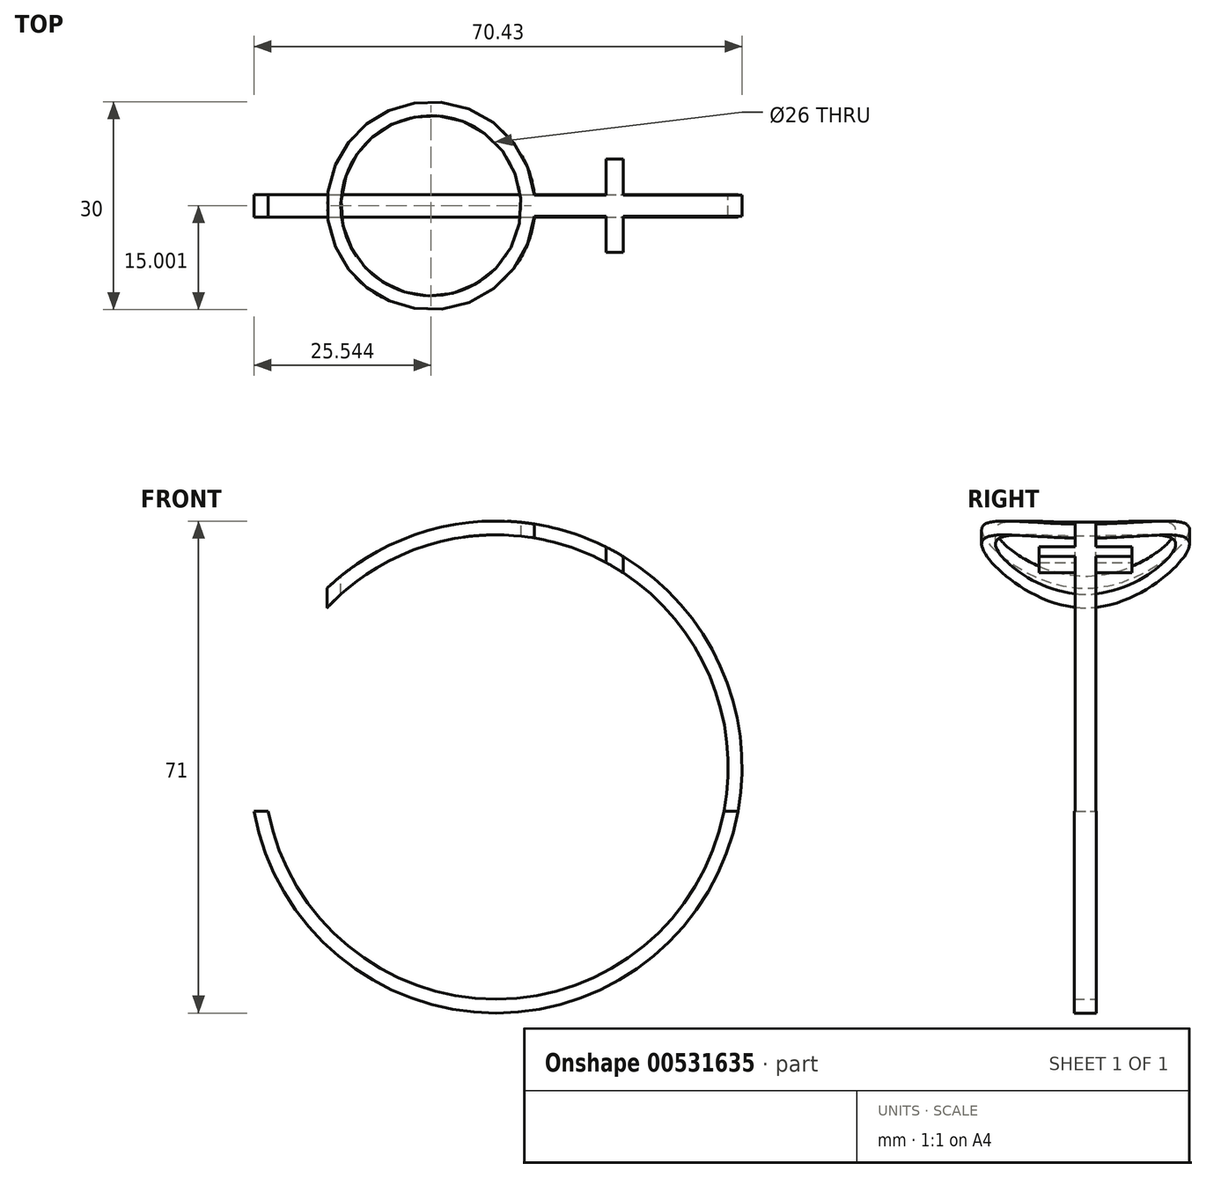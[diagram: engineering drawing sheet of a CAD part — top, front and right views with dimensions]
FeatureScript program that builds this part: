
annotation { "Feature Type Name" : "Feature", "Feature Type Description" : "" }
export const myFeature = defineFeature(function(context is Context, id is Id, definition is map)
    precondition{}
    {
        {
            var Q0;
            Q0=qCreatedBy(makeId("Front.planeOp"),FACE);
            var sketch = newSketch(context, id + "F0", { "sketchPlane" : qUnion([Q0])});
            skCircle(sketch, "E0", {"center": v(0, 0) * mm, "radius": 33.5 * mm});
            skCircle(sketch, "E1", {"center": v(0, 0) * mm, "radius": 35.5 * mm});
            skSolve(sketch);
        }
        {
            var Q0;
            Q0=makeQuery(id+"F0.imprint","IMPRINT",FACE,{"disambiguationData":[TD([[makeQuery(id+"F0.imprint","IMPRINT",EDGE,{"derivedFrom":sQuery(id+"F0.wireOp",EDGE,"E0")}),-1.0]])]});
            extrude(context, id + "F1", {"entities" : qUnion([Q0]), "depth" : 50.8 * mm, "offsetDistance" : 25.4 * mm});
        }
        {
            var Q0;
            Q0=qCreatedBy(makeId("Top.planeOp"),FACE);
            cPlane(context, id + "F2", {"entities" : qUnion([Q0]), "cplaneType" : CPlaneType.OFFSET, "offset" : 38.1 * mm, "width" : 152.4 * mm, "height" : 152.4 * mm});
        }
        {
            var Q0;
            Q0=qCreatedBy(id+"F2.planeOp",FACE);
            var sketch = newSketch(context, id + "F3", { "sketchPlane" : qUnion([Q0])});
            skCircle(sketch, "E2", {"center": v(-9.39, -26.8) * mm, "radius": 15 * mm});
            skCircle(sketch, "E3", {"center": v(-9.39, -26.8) * mm, "radius": 13 * mm});
            skLineSegment(sketch, "E4", {"start": v(5.61, -26.8) * mm, "end": v(11.46, -26.8) * mm});
            skLineSegment(sketch, "E5", {"start": v(5.54, -28.3) * mm, "end": v(15.85, -28.3) * mm});
            skLineSegment(sketch, "E6", {"start": v(15.85, -28.3) * mm, "end": v(15.85, -33.5) * mm});
            skLineSegment(sketch, "E7", {"start": v(15.85, -33.5) * mm, "end": v(18.35, -33.5) * mm});
            skLineSegment(sketch, "E8", {"start": v(18.35, -33.5) * mm, "end": v(18.35, -28.3) * mm});
            skLineSegment(sketch, "E9", {"start": v(18.35, -28.3) * mm, "end": v(35.63, -28.3) * mm});
            skLineSegment(sketch, "E10", {"start": v(35.63, -28.3) * mm, "end": v(35.63, -26.8) * mm});
            skLineSegment(sketch, "E11.MirrorCS", {"start": v(5.54, -25.3) * mm, "end": v(15.85, -25.3) * mm});
            skLineSegment(sketch, "E12.MirrorCS", {"start": v(15.85, -25.3) * mm, "end": v(15.85, -20.1) * mm});
            skLineSegment(sketch, "E13.MirrorCS", {"start": v(15.85, -20.1) * mm, "end": v(18.35, -20.1) * mm});
            skLineSegment(sketch, "E14.MirrorCS", {"start": v(18.35, -20.1) * mm, "end": v(18.35, -25.3) * mm});
            skLineSegment(sketch, "E15.MirrorCS", {"start": v(18.35, -25.3) * mm, "end": v(35.63, -25.3) * mm});
            skLineSegment(sketch, "E16.MirrorCS", {"start": v(35.63, -25.3) * mm, "end": v(35.63, -26.8) * mm});
            skLineSegment(sketch, "E17", {"start": v(15.85, -25.3) * mm, "end": v(18.35, -25.3) * mm});
            skLineSegment(sketch, "E18", {"start": v(18.35, -28.3) * mm, "end": v(15.85, -28.3) * mm});
            skLineSegment(sketch, "E19", {"start": v(35.63, -25.3) * mm, "end": v(35.63, 3.78) * mm});
            skLineSegment(sketch, "E20", {"start": v(35.63, 3.78) * mm, "end": v(-42.06, 3.78) * mm});
            skLineSegment(sketch, "E21", {"start": v(-42.06, 3.78) * mm, "end": v(-40.55, -55.05) * mm});
            skLineSegment(sketch, "E22", {"start": v(-40.55, -55.05) * mm, "end": v(35.63, -53.1) * mm});
            skLineSegment(sketch, "E23", {"start": v(35.63, -53.1) * mm, "end": v(35.63, -28.3) * mm});
            skSolve(sketch);
        }
        {
            var Q0;
            {var subQ1=sQuery(id+"F3.wireOp",EDGE,"E5");Q0=makeQuery(id+"F3.imprint","IMPRINT",FACE,{"disambiguationData":[TD([[makeQuery(id+"F3.imprint","IMPRINT",EDGE,{"derivedFrom":subQ1}),-1.0]])]});}
            var Q1;
            Q1=makeQuery(id+"F3.imprint","IMPRINT",FACE,{"disambiguationData":[TD([[makeQuery(id+"F3.imprint","IMPRINT",EDGE,{"derivedFrom":sQuery(id+"F3.wireOp",EDGE,"E3")}),1.0]])]});
            extrude(context, id + "F4", {"entities" : qUnion([Q0, Q1]), "operationType" : NewBodyOperationType.REMOVE, "oppositeDirection" : true, "depth" : 44.45 * mm, "offsetDistance" : 25.4 * mm});
        }
        {
            var Q0;
            Q0=qCreatedBy(makeId("Right.planeOp"),FACE);
            var sketch = newSketch(context, id + "F5", { "sketchPlane" : qUnion([Q0])});
            skLineSegment(sketch, "E24", {"start": v(-28.45, -6.05) * mm, "end": v(-28.45, -37.6) * mm});
            skLineSegment(sketch, "E25", {"start": v(-28.45, -37.6) * mm, "end": v(-52.3, -37.6) * mm});
            skLineSegment(sketch, "E26", {"start": v(-52.3, -37.6) * mm, "end": v(-52.3, -5.73) * mm});
            skLineSegment(sketch, "E27", {"start": v(-52.3, -5.73) * mm, "end": v(-28.45, -6.05) * mm});
            skLineSegment(sketch, "E28", {"start": v(-25.25, -6.05) * mm, "end": v(-25.25, -37.27) * mm});
            skLineSegment(sketch, "E29", {"start": v(-25.25, -37.27) * mm, "end": v(5.4, -37.68) * mm});
            skLineSegment(sketch, "E30", {"start": v(5.4, -37.68) * mm, "end": v(4.12, -6.05) * mm});
            skLineSegment(sketch, "E31", {"start": v(4.12, -6.05) * mm, "end": v(-25.25, -6.05) * mm});
            skSolve(sketch);
        }
        {
            var Q0;
            Q0=makeQuery(id+"F5.imprint","IMPRINT",FACE,{"disambiguationData":[TD([[makeQuery(id+"F5.imprint","IMPRINT",EDGE,{"derivedFrom":sQuery(id+"F5.wireOp",EDGE,"E24")}),-1.0]])]});
            var Q1;
            Q1=makeQuery(id+"F5.imprint","IMPRINT",FACE,{"disambiguationData":[TD([[makeQuery(id+"F5.imprint","IMPRINT",EDGE,{"derivedFrom":sQuery(id+"F5.wireOp",EDGE,"E28")}),1.0]])]});
            extrude(context, id + "F6", {"entities" : qUnion([Q0, Q1]), "operationType" : NewBodyOperationType.REMOVE, "endBound" : BoundingType.SYMMETRIC, "oppositeDirection" : true, "depth" : 76.2 * mm, "offsetDistance" : 25.4 * mm});
        }
    });
